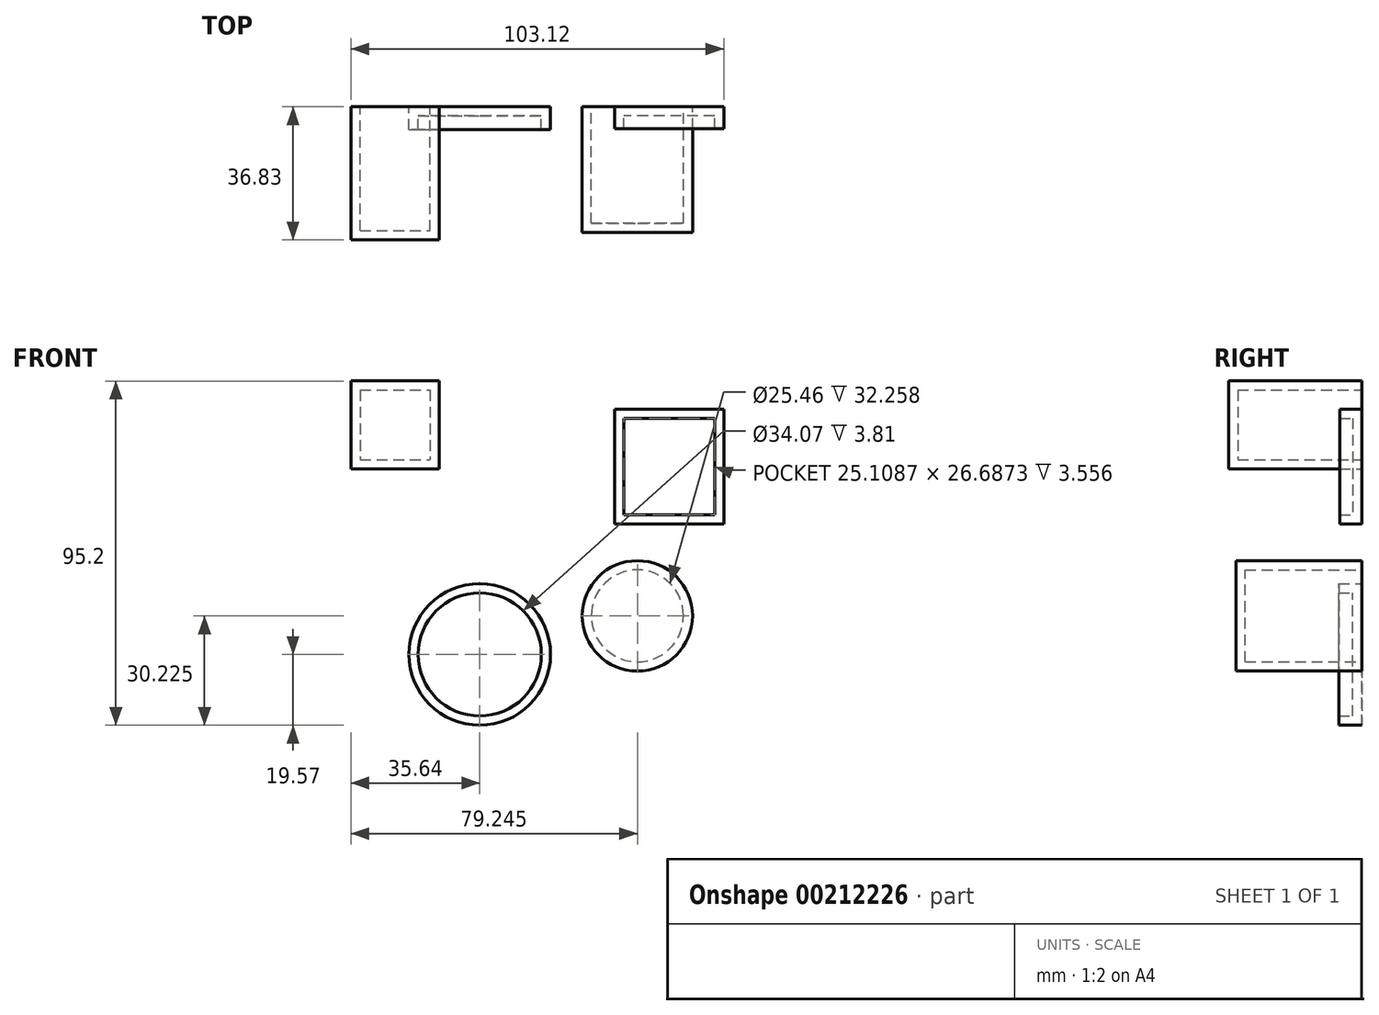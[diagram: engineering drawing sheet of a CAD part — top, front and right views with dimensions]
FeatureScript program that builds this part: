
annotation { "Feature Type Name" : "Feature", "Feature Type Description" : "" }
export const myFeature = defineFeature(function(context is Context, id is Id, definition is map)
    precondition{}
    {
        {
            var Q0;
            Q0=qCreatedBy(makeId("Front.planeOp"),FACE);
            var sketch = newSketch(context, id + "F0", { "sketchPlane" : qUnion([Q0])});
            skLineSegment(sketch, "E0.bottom", {"start": v(-56.16, 42.58) * mm, "end": v(-31.77, 42.58) * mm});
            skLineSegment(sketch, "E0.top", {"start": v(-56.16, 18.2) * mm, "end": v(-31.77, 18.2) * mm});
            skLineSegment(sketch, "E0.left", {"start": v(-56.16, 42.58) * mm, "end": v(-56.16, 18.2) * mm});
            skLineSegment(sketch, "E0.right", {"start": v(-31.77, 42.58) * mm, "end": v(-31.77, 18.2) * mm});
            skSolve(sketch);
        }
        {
            var Q0;
            Q0 = qSketchRegion(id + "F0", true);
            extrude(context, id + "F1", {"entities" : qUnion([Q0]), "depth" : 36.83 * mm});
        }
        {
            var Q0;
            Q0=makeQuery(id+"F1.opExtrude","CAP_FACE",FACE,{"disambiguationData":[OSD([sQuery(id+"F0.wireOp",EDGE,"E0.bottom"),sQuery(id+"F0.wireOp",EDGE,"E0.top"),sQuery(id+"F0.wireOp",EDGE,"E0.left"),sQuery(id+"F0.wireOp",EDGE,"E0.right")])],"isStart":true});
            shell(context, id + "F2", {"entities" : qUnion([Q0]), "thickness" : 2.54 * mm});
        }
        {
            var Q0;
            Q0=qCreatedBy(makeId("Front.planeOp"),FACE);
            var sketch = newSketch(context, id + "F3", { "sketchPlane" : qUnion([Q0])});
            skLineSegment(sketch, "E1.bottom", {"start": v(46.96, 34.83) * mm, "end": v(16.77, 34.83) * mm});
            skLineSegment(sketch, "E1.top", {"start": v(46.96, 3.06) * mm, "end": v(16.77, 3.06) * mm});
            skLineSegment(sketch, "E1.left", {"start": v(46.96, 34.83) * mm, "end": v(46.96, 3.06) * mm});
            skLineSegment(sketch, "E1.right", {"start": v(16.77, 34.83) * mm, "end": v(16.77, 3.06) * mm});
            skSolve(sketch);
        }
        {
            var Q0;
            Q0 = qSketchRegion(id + "F3", true);
            extrude(context, id + "F4", {"entities" : qUnion([Q0]), "depth" : 6.1 * mm});
        }
        {
            var Q0;
            Q0=makeQuery(id+"F4.opExtrude","CAP_FACE",FACE,{"disambiguationData":[OSD([sQuery(id+"F3.wireOp",EDGE,"E1.bottom"),sQuery(id+"F3.wireOp",EDGE,"E1.top"),sQuery(id+"F3.wireOp",EDGE,"E1.left"),sQuery(id+"F3.wireOp",EDGE,"E1.right")])],"isStart":false});
            shell(context, id + "F5", {"entities" : qUnion([Q0]), "thickness" : 2.54 * mm});
        }
        {
            var Q0;
            Q0=qCreatedBy(makeId("Front.planeOp"),FACE);
            var sketch = newSketch(context, id + "F6", { "sketchPlane" : qUnion([Q0])});
            skCircle(sketch, "E2", {"center": v(-20.52, -33.05) * mm, "radius": 19.57 * mm});
            skSolve(sketch);
        }
        {
            var Q0;
            Q0=makeQuery(id+"F6.imprint","IMPRINT",FACE,{"disambiguationData":[TD([[makeQuery(id+"F6.imprint","IMPRINT",EDGE,{"derivedFrom":sQuery(id+"F6.wireOp",EDGE,"E2")}),1.0]])]});
            extrude(context, id + "F7", {"entities" : qUnion([Q0]), "depth" : 6.35 * mm});
        }
        {
            var Q0;
            Q0=makeQuery(id+"F7.opExtrude","CAP_FACE",FACE,{"disambiguationData":[OSD([sQuery(id+"F6.wireOp",EDGE,"E2")])],"isStart":false});
            shell(context, id + "F8", {"entities" : qUnion([Q0]), "thickness" : 2.54 * mm});
        }
        {
            var Q0;
            Q0=qCreatedBy(makeId("Front.planeOp"),FACE);
            var sketch = newSketch(context, id + "F9", { "sketchPlane" : qUnion([Q0])});
            skCircle(sketch, "E3", {"center": v(23.09, -22.4) * mm, "radius": 15.27 * mm});
            skSolve(sketch);
        }
        {
            var Q0;
            Q0 = qSketchRegion(id + "F9", true);
            extrude(context, id + "F10", {"entities" : qUnion([Q0]), "depth" : 34.8 * mm});
        }
        {
            var Q0;
            Q0=makeQuery(id+"F10.opExtrude","CAP_FACE",FACE,{"disambiguationData":[OSD([sQuery(id+"F9.wireOp",EDGE,"E3")])],"isStart":true});
            shell(context, id + "F11", {"entities" : qUnion([Q0]), "thickness" : 2.54 * mm});
        }
    });
